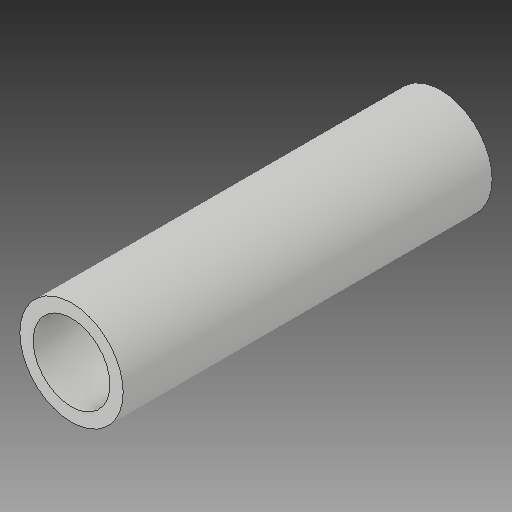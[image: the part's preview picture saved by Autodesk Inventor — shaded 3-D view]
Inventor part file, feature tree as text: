
AUTODESK INVENTOR PART (.ipt)
format: ipt  version: 2018 (Build 220112000, 112)  size: 100,352 bytes
history: native  units: mm
features: other x4, extrude x1, sketch x1, reference x1
ambient origin geometry x8: Origin, YZ Plane, XZ Plane, XY Plane, X Axis, Y Axis, Z Axis, Center Point
bodies: Solid1 (feature_tree)
feature tree (7):
  extrude  "Extrusion1"  Depth=25.0mm
  sketch  "Sketch1"  dims[d0=5.2mm d1=7.0mm d2=25.0mm d3=0.0mm]
  reference  "Reference1"
  parser-record x1  (decoder bookkeeping rows leaked as tree rows — omitted from the tree; the rows remain in map.json)
  other  "Main assembly Test.iam"
  other  "3030bracket_MIR_MIR:2"
  other  "Forged Socket Head Cap Screw - Metric M5x0.8 x 12:1"
note: 1 file-system path scrubbed to <path> (originals preserved in map.json)
